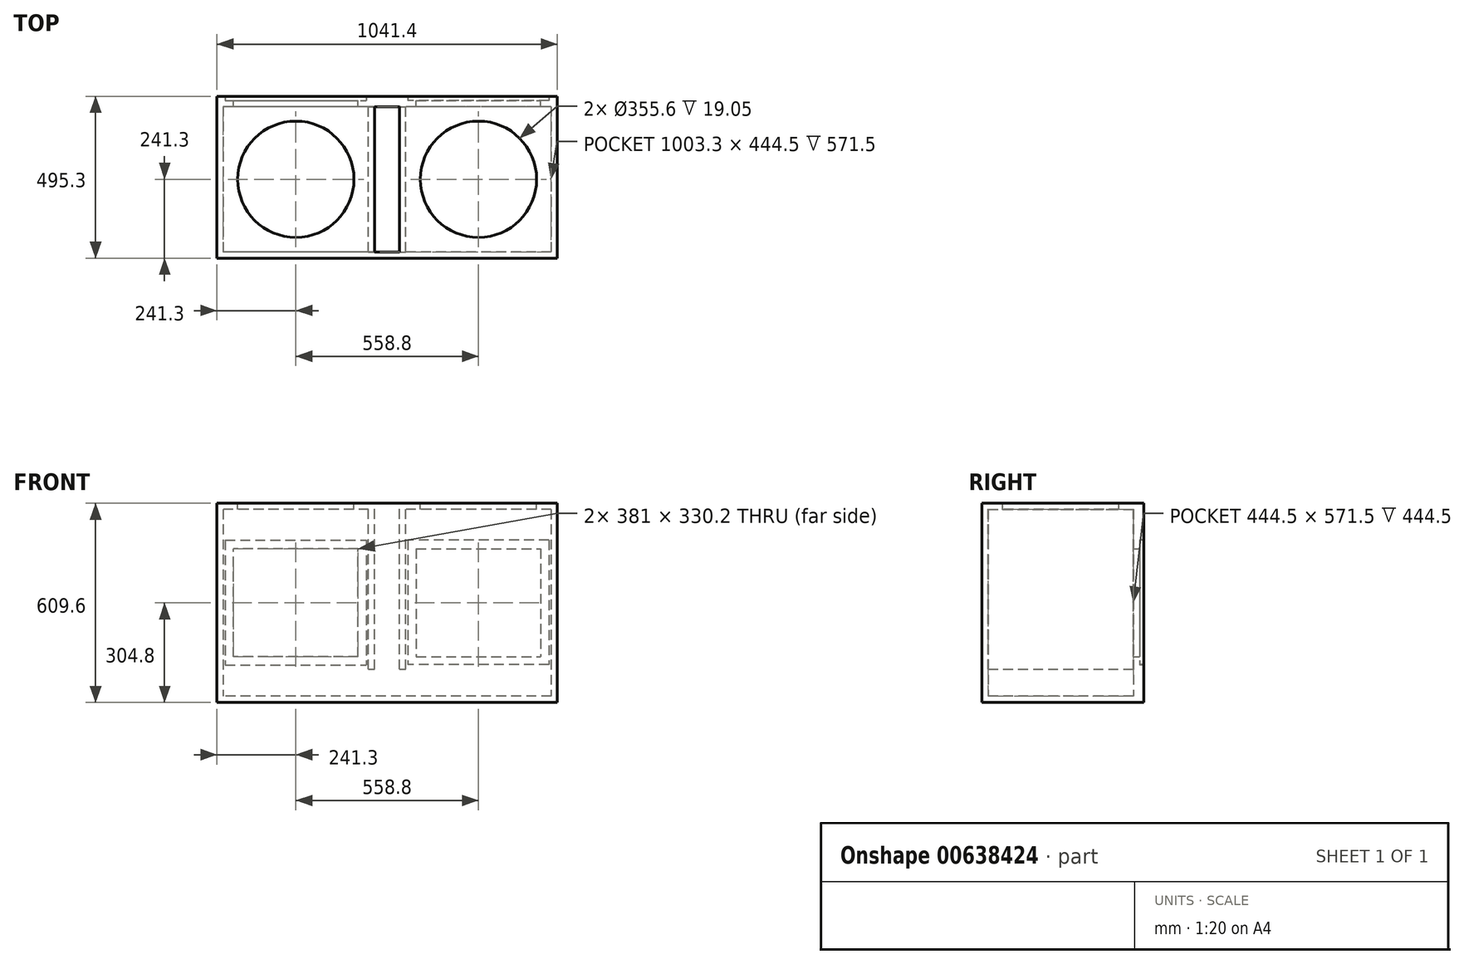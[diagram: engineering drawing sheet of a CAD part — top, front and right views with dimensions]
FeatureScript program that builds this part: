
annotation { "Feature Type Name" : "Feature", "Feature Type Description" : "" }
export const myFeature = defineFeature(function(context is Context, id is Id, definition is map)
    precondition{}
    {
        {
            var Q0;
            Q0=qCreatedBy(makeId("Top.planeOp"),FACE);
            var sketch = newSketch(context, id + "F0", { "sketchPlane" : qUnion([Q0])});
            skLineSegment(sketch, "E0.bottom", {"start": v(520.7, 241.3) * mm, "end": v(-520.7, 241.3) * mm});
            skLineSegment(sketch, "E0.top", {"start": v(520.7, -241.3) * mm, "end": v(-520.7, -241.3) * mm});
            skLineSegment(sketch, "E0.left", {"start": v(520.7, 241.3) * mm, "end": v(520.7, -241.3) * mm});
            skLineSegment(sketch, "E0.right", {"start": v(-520.7, 241.3) * mm, "end": v(-520.7, -241.3) * mm});
            skPoint(sketch, "E0.middle", {"position": v(0, 0) * mm});
            skSolve(sketch);
        }
        {
            var Q0;
            Q0=makeQuery(id+"F0.imprint","IMPRINT",FACE,{"disambiguationData":[TD([[makeQuery(id+"F0.imprint","IMPRINT",EDGE,{"derivedFrom":sQuery(id+"F0.wireOp",EDGE,"E0.bottom")}),1.0]])]});
            extrude(context, id + "F1", {"entities" : qUnion([Q0]), "depth" : 304.8 * mm, "offsetDistance" : 25.4 * mm, "hasSecondDirection" : true, "secondDirectionOppositeDirection" : true, "secondDirectionDepth" : 304.8 * mm});
        }
        {
            var Q0;
            Q0=makeQuery(id+"F1.opExtrude","CAP_FACE",FACE,{"disambiguationData":[OSD([sQuery(id+"F0.wireOp",EDGE,"E0.bottom"),sQuery(id+"F0.wireOp",EDGE,"E0.top"),sQuery(id+"F0.wireOp",EDGE,"E0.left"),sQuery(id+"F0.wireOp",EDGE,"E0.right")])],"isStart":false});
            shell(context, id + "F2", {"entities" : qUnion([Q0]), "thickness" : 19.05 * mm});
        }
        {
            var Q0;
            Q0=makeQuery(id+"F1.opExtrude","SWEPT_FACE",FACE,{"disambiguationData":[OSD([sQuery(id+"F0.wireOp",EDGE,"E0.bottom")])]});
            var sketch = newSketch(context, id + "F3", { "sketchPlane" : qUnion([Q0])});
            skLineSegment(sketch, "E1.bottom", {"start": v(-88.9, 165.1) * mm, "end": v(-469.9, 165.1) * mm});
            skLineSegment(sketch, "E1.top", {"start": v(-88.9, -165.1) * mm, "end": v(-469.9, -165.1) * mm});
            skLineSegment(sketch, "E1.left", {"start": v(-88.9, 165.1) * mm, "end": v(-88.9, -165.1) * mm});
            skLineSegment(sketch, "E1.right", {"start": v(-469.9, 165.1) * mm, "end": v(-469.9, -165.1) * mm});
            skLineSegment(sketch, "E2.bottom", {"start": v(469.9, 165.1) * mm, "end": v(88.9, 165.1) * mm});
            skLineSegment(sketch, "E2.top", {"start": v(469.9, -165.1) * mm, "end": v(88.9, -165.1) * mm});
            skLineSegment(sketch, "E2.left", {"start": v(469.9, 165.1) * mm, "end": v(469.9, -165.1) * mm});
            skLineSegment(sketch, "E2.right", {"start": v(88.9, 165.1) * mm, "end": v(88.9, -165.1) * mm});
            skPoint(sketch, "E3", {"position": v(0, 0) * mm});
            skSolve(sketch);
        }
        {
            var Q0;
            Q0=makeQuery(id+"F3.imprint","IMPRINT",FACE,{"disambiguationData":[TD([[makeQuery(id+"F3.imprint","IMPRINT",EDGE,{"derivedFrom":sQuery(id+"F3.wireOp",EDGE,"E1.bottom")}),1.0]])]});
            var Q1;
            Q1=makeQuery(id+"F3.imprint","IMPRINT",FACE,{"disambiguationData":[TD([[makeQuery(id+"F3.imprint","IMPRINT",EDGE,{"derivedFrom":sQuery(id+"F3.wireOp",EDGE,"E2.bottom")}),1.0]])]});
            extrude(context, id + "F4", {"entities" : qUnion([Q0, Q1]), "operationType" : NewBodyOperationType.REMOVE, "oppositeDirection" : true, "depth" : 25.4 * mm, "offsetDistance" : 25.4 * mm});
        }
        {
            var Q0;
            Q0=makeQuery(id+"F1.opExtrude","CAP_FACE",FACE,{"disambiguationData":[OSD([sQuery(id+"F0.wireOp",EDGE,"E0.bottom"),sQuery(id+"F0.wireOp",EDGE,"E0.top"),sQuery(id+"F0.wireOp",EDGE,"E0.left"),sQuery(id+"F0.wireOp",EDGE,"E0.right")])],"isStart":false});
            var sketch = newSketch(context, id + "F5", { "sketchPlane" : qUnion([Q0])});
            skPoint(sketch, "E4", {"position": v(0, 0) * mm});
            skLineSegment(sketch, "E5.bottom", {"start": v(501.65, -222.25) * mm, "end": v(-501.65, -222.25) * mm});
            skLineSegment(sketch, "E5.top", {"start": v(501.65, 222.25) * mm, "end": v(-501.65, 222.25) * mm});
            skLineSegment(sketch, "E5.left", {"start": v(501.65, -222.25) * mm, "end": v(501.65, 222.25) * mm});
            skLineSegment(sketch, "E5.right", {"start": v(-501.65, -222.25) * mm, "end": v(-501.65, 222.25) * mm});
            skSolve(sketch);
        }
        {
            var Q0;
            Q0=makeQuery(id+"F5.imprint","IMPRINT",FACE,{"disambiguationData":[TD([[makeQuery(id+"F5.imprint","IMPRINT",EDGE,{"derivedFrom":sQuery(id+"F5.wireOp",EDGE,"E5.bottom")}),-1.0]])]});
            extrude(context, id + "F6", {"entities" : qUnion([Q0]), "operationType" : NewBodyOperationType.ADD, "depth" : 0 * mm, "offsetDistance" : 25.4 * mm, "hasSecondDirection" : true, "secondDirectionOppositeDirection" : true, "secondDirectionDepth" : 19.05 * mm});
        }
        {
            var Q0;
            Q0=makeQuery(id+"F6.boolean.opBoolean","MERGE",FACE,{"derivedFrom":[makeQuery(id+"F1.opExtrude","CAP_FACE",FACE,{"disambiguationData":[OSD([sQuery(id+"F0.wireOp",EDGE,"E0.bottom"),sQuery(id+"F0.wireOp",EDGE,"E0.top"),sQuery(id+"F0.wireOp",EDGE,"E0.left"),sQuery(id+"F0.wireOp",EDGE,"E0.right")])],"isStart":false}),makeQuery(id+"F6.opExtrude","CAP_FACE",FACE,{"disambiguationData":[OSD([sQuery(id+"F5.wireOp",EDGE,"E5.bottom"),sQuery(id+"F5.wireOp",EDGE,"E5.top"),sQuery(id+"F5.wireOp",EDGE,"E5.left"),sQuery(id+"F5.wireOp",EDGE,"E5.right")])],"isStart":false})]});
            var sketch = newSketch(context, id + "F7", { "sketchPlane" : qUnion([Q0])});
            skPoint(sketch, "E6", {"position": v(0, 0) * mm});
            skLineSegment(sketch, "E7", {"start": v(0, 0) * mm, "end": v(38.1, 0) * mm});
            skLineSegment(sketch, "E8", {"start": v(38.1, 0) * mm, "end": v(-38.1, 0) * mm});
            skLineSegment(sketch, "E9.bottom", {"start": v(-38.1, -222.25) * mm, "end": v(38.1, -222.25) * mm});
            skLineSegment(sketch, "E9.top", {"start": v(-38.1, 222.25) * mm, "end": v(38.1, 222.25) * mm});
            skLineSegment(sketch, "E9.left", {"start": v(-38.1, -222.25) * mm, "end": v(-38.1, 222.25) * mm});
            skLineSegment(sketch, "E9.right", {"start": v(38.1, -222.25) * mm, "end": v(38.1, 222.25) * mm});
            skSolve(sketch);
        }
        {
            var Q0;
            Q0 = qSketchRegion(id + "F7", true);
            extrude(context, id + "F8", {"entities" : qUnion([Q0]), "operationType" : NewBodyOperationType.REMOVE, "oppositeDirection" : true, "depth" : 25.4 * mm, "offsetDistance" : 25.4 * mm});
        }
        {
            var Q0;
            Q0=makeQuery(id+"F6.boolean.opBoolean","MERGE",FACE,{"derivedFrom":[makeQuery(id+"F1.opExtrude","CAP_FACE",FACE,{"disambiguationData":[OSD([sQuery(id+"F0.wireOp",EDGE,"E0.bottom"),sQuery(id+"F0.wireOp",EDGE,"E0.top"),sQuery(id+"F0.wireOp",EDGE,"E0.left"),sQuery(id+"F0.wireOp",EDGE,"E0.right")])],"isStart":false}),makeQuery(id+"F6.opExtrude","CAP_FACE",FACE,{"disambiguationData":[OSD([sQuery(id+"F5.wireOp",EDGE,"E5.bottom"),sQuery(id+"F5.wireOp",EDGE,"E5.top"),sQuery(id+"F5.wireOp",EDGE,"E5.left"),sQuery(id+"F5.wireOp",EDGE,"E5.right")])],"isStart":false})]});
            var sketch = newSketch(context, id + "F9", { "sketchPlane" : qUnion([Q0])});
            skCircle(sketch, "E10", {"center": v(279.4, 0) * mm, "radius": 177.8 * mm});
            skCircle(sketch, "E11", {"center": v(-279.4, 0) * mm, "radius": 177.8 * mm});
            skSolve(sketch);
        }
        {
            var Q0;
            Q0=makeQuery(id+"F9.imprint","IMPRINT",FACE,{"disambiguationData":[TD([[makeQuery(id+"F9.imprint","IMPRINT",EDGE,{"derivedFrom":sQuery(id+"F9.wireOp",EDGE,"E11")}),1.0]])]});
            var Q1;
            Q1=makeQuery(id+"F9.imprint","IMPRINT",FACE,{"disambiguationData":[TD([[makeQuery(id+"F9.imprint","IMPRINT",EDGE,{"derivedFrom":sQuery(id+"F9.wireOp",EDGE,"E10")}),1.0]])]});
            extrude(context, id + "F10", {"entities" : qUnion([Q0, Q1]), "operationType" : NewBodyOperationType.REMOVE, "oppositeDirection" : true, "depth" : 25.4 * mm, "offsetDistance" : 25.4 * mm});
        }
        {
            var Q0;
            Q0=makeQuery(id+"F6.boolean.opBoolean","MERGE",FACE,{"derivedFrom":[makeQuery(id+"F1.opExtrude","CAP_FACE",FACE,{"disambiguationData":[OSD([sQuery(id+"F0.wireOp",EDGE,"E0.bottom"),sQuery(id+"F0.wireOp",EDGE,"E0.top"),sQuery(id+"F0.wireOp",EDGE,"E0.left"),sQuery(id+"F0.wireOp",EDGE,"E0.right")])],"isStart":false}),makeQuery(id+"F6.opExtrude","CAP_FACE",FACE,{"disambiguationData":[OSD([sQuery(id+"F5.wireOp",EDGE,"E5.bottom"),sQuery(id+"F5.wireOp",EDGE,"E5.top"),sQuery(id+"F5.wireOp",EDGE,"E5.left"),sQuery(id+"F5.wireOp",EDGE,"E5.right")])],"isStart":false})]});
            var sketch = newSketch(context, id + "F11", { "sketchPlane" : qUnion([Q0])});
            skLineSegment(sketch, "E12.bottom", {"start": v(-57.15, -222.25) * mm, "end": v(-38.1, -222.25) * mm});
            skLineSegment(sketch, "E12.top", {"start": v(-57.15, 222.25) * mm, "end": v(-38.1, 222.25) * mm});
            skLineSegment(sketch, "E12.left", {"start": v(-57.15, -222.25) * mm, "end": v(-57.15, 222.25) * mm});
            skLineSegment(sketch, "E12.right", {"start": v(-38.1, -222.25) * mm, "end": v(-38.1, 222.25) * mm});
            skSolve(sketch);
        }
        {
            var Q0;
            Q0=makeQuery(id+"F11.imprint","IMPRINT",FACE,{"disambiguationData":[TD([[makeQuery(id+"F11.imprint","IMPRINT",EDGE,{"derivedFrom":sQuery(id+"F11.wireOp",EDGE,"E12.bottom")}),1.0]])]});
            extrude(context, id + "F12", {"entities" : qUnion([Q0]), "operationType" : NewBodyOperationType.ADD, "depth" : 0 * mm, "offsetDistance" : 25.4 * mm, "hasSecondDirection" : true, "secondDirectionOppositeDirection" : true, "secondDirectionDepth" : 508 * mm});
        }
        {
            var Q0;
            Q0=makeQuery(id+"F6.boolean.opBoolean","MERGE",FACE,{"derivedFrom":[makeQuery(id+"F1.opExtrude","CAP_FACE",FACE,{"disambiguationData":[OSD([sQuery(id+"F0.wireOp",EDGE,"E0.bottom"),sQuery(id+"F0.wireOp",EDGE,"E0.top"),sQuery(id+"F0.wireOp",EDGE,"E0.left"),sQuery(id+"F0.wireOp",EDGE,"E0.right")])],"isStart":false}),makeQuery(id+"F6.opExtrude","CAP_FACE",FACE,{"disambiguationData":[OSD([sQuery(id+"F5.wireOp",EDGE,"E5.bottom"),sQuery(id+"F5.wireOp",EDGE,"E5.top"),sQuery(id+"F5.wireOp",EDGE,"E5.left"),sQuery(id+"F5.wireOp",EDGE,"E5.right")])],"isStart":false})]});
            var sketch = newSketch(context, id + "F13", { "sketchPlane" : qUnion([Q0])});
            skLineSegment(sketch, "E13", {"start": v(38.1, 0) * mm, "end": v(47.63, 0) * mm});
            skPoint(sketch, "E14", {"position": v(47.63, 0) * mm});
            skLineSegment(sketch, "E15.bottom", {"start": v(38.1, -222.25) * mm, "end": v(57.15, -222.25) * mm});
            skLineSegment(sketch, "E15.top", {"start": v(38.1, 222.25) * mm, "end": v(57.15, 222.25) * mm});
            skLineSegment(sketch, "E15.left", {"start": v(38.1, -222.25) * mm, "end": v(38.1, 222.25) * mm});
            skLineSegment(sketch, "E15.right", {"start": v(57.15, -222.25) * mm, "end": v(57.15, 222.25) * mm});
            skSolve(sketch);
        }
        {
            var Q0;
            Q0 = qSketchRegion(id + "F13", true);
            extrude(context, id + "F14", {"entities" : qUnion([Q0]), "operationType" : NewBodyOperationType.ADD, "depth" : 0 * mm, "offsetDistance" : 25.4 * mm, "hasSecondDirection" : true, "secondDirectionOppositeDirection" : true, "secondDirectionDepth" : 508 * mm});
        }
        {
            var Q0;
            Q0=makeQuery(id+"F1.opExtrude","SWEPT_FACE",FACE,{"disambiguationData":[OSD([sQuery(id+"F0.wireOp",EDGE,"E0.bottom")])]});
            var sketch = newSketch(context, id + "F15", { "sketchPlane" : qUnion([Q0])});
            skSolve(sketch);
        }
        {
            var Q0;
            {var subQ0=sQuery(id+"F0.wireOp",EDGE,"E0.bottom");Q0=makeQuery(id+"F15.imprint","IMPRINT",FACE,{"disambiguationData":[TD([[makeQuery(id+"F15.imprint","IMPRINT",EDGE,{"derivedFrom":makeQuery(id+"F1.opExtrude","CAP_EDGE",EDGE,{"disambiguationData":[OSD([subQ0])],"isStart":true})}),1.0]])]});}
            var sketch = newSketch(context, id + "F16", { "sketchPlane" : qUnion([Q0])});
            skPoint(sketch, "E16", {"position": v(-520.7, 304.8) * mm});
            skPoint(sketch, "E17", {"position": v(520.7, -304.8) * mm});
            skLineSegment(sketch, "E18.bottom", {"start": v(-520.7, 304.8) * mm, "end": v(520.7, 304.8) * mm});
            skLineSegment(sketch, "E18.top", {"start": v(-520.7, -304.8) * mm, "end": v(520.7, -304.8) * mm});
            skLineSegment(sketch, "E18.left", {"start": v(-520.7, 304.8) * mm, "end": v(-520.7, -304.8) * mm});
            skLineSegment(sketch, "E18.right", {"start": v(520.7, 304.8) * mm, "end": v(520.7, -304.8) * mm});
            skPoint(sketch, "E19", {"position": v(-494.84, 191.81) * mm});
            skPoint(sketch, "E20", {"position": v(-63.04, -189.19) * mm});
            skLineSegment(sketch, "E21.bottom", {"start": v(-494.84, 191.81) * mm, "end": v(-63.04, 191.81) * mm});
            skLineSegment(sketch, "E21.top", {"start": v(-494.84, -189.19) * mm, "end": v(-63.04, -189.19) * mm});
            skLineSegment(sketch, "E21.left", {"start": v(-494.84, 191.81) * mm, "end": v(-494.84, -189.19) * mm});
            skLineSegment(sketch, "E21.right", {"start": v(-63.04, 191.81) * mm, "end": v(-63.04, -189.19) * mm});
            skPoint(sketch, "E22", {"position": v(495.24, 191.39) * mm});
            skLineSegment(sketch, "E23.bottom", {"start": v(495.24, 191.39) * mm, "end": v(63.43, 191.39) * mm});
            skLineSegment(sketch, "E23.top", {"start": v(495.24, -190.43) * mm, "end": v(63.43, -190.43) * mm});
            skLineSegment(sketch, "E23.left", {"start": v(495.24, 191.39) * mm, "end": v(495.24, -190.43) * mm});
            skLineSegment(sketch, "E23.right", {"start": v(63.43, 191.39) * mm, "end": v(63.43, -190.43) * mm});
            skSolve(sketch);
        }
        {
            var Q0;
            Q0 = qSketchRegion(id + "F16", true);
            extrude(context, id + "F17", {"entities" : qUnion([Q0]), "operationType" : NewBodyOperationType.ADD, "depth" : 12.7 * mm, "offsetDistance" : 25.4 * mm});
        }
    });
